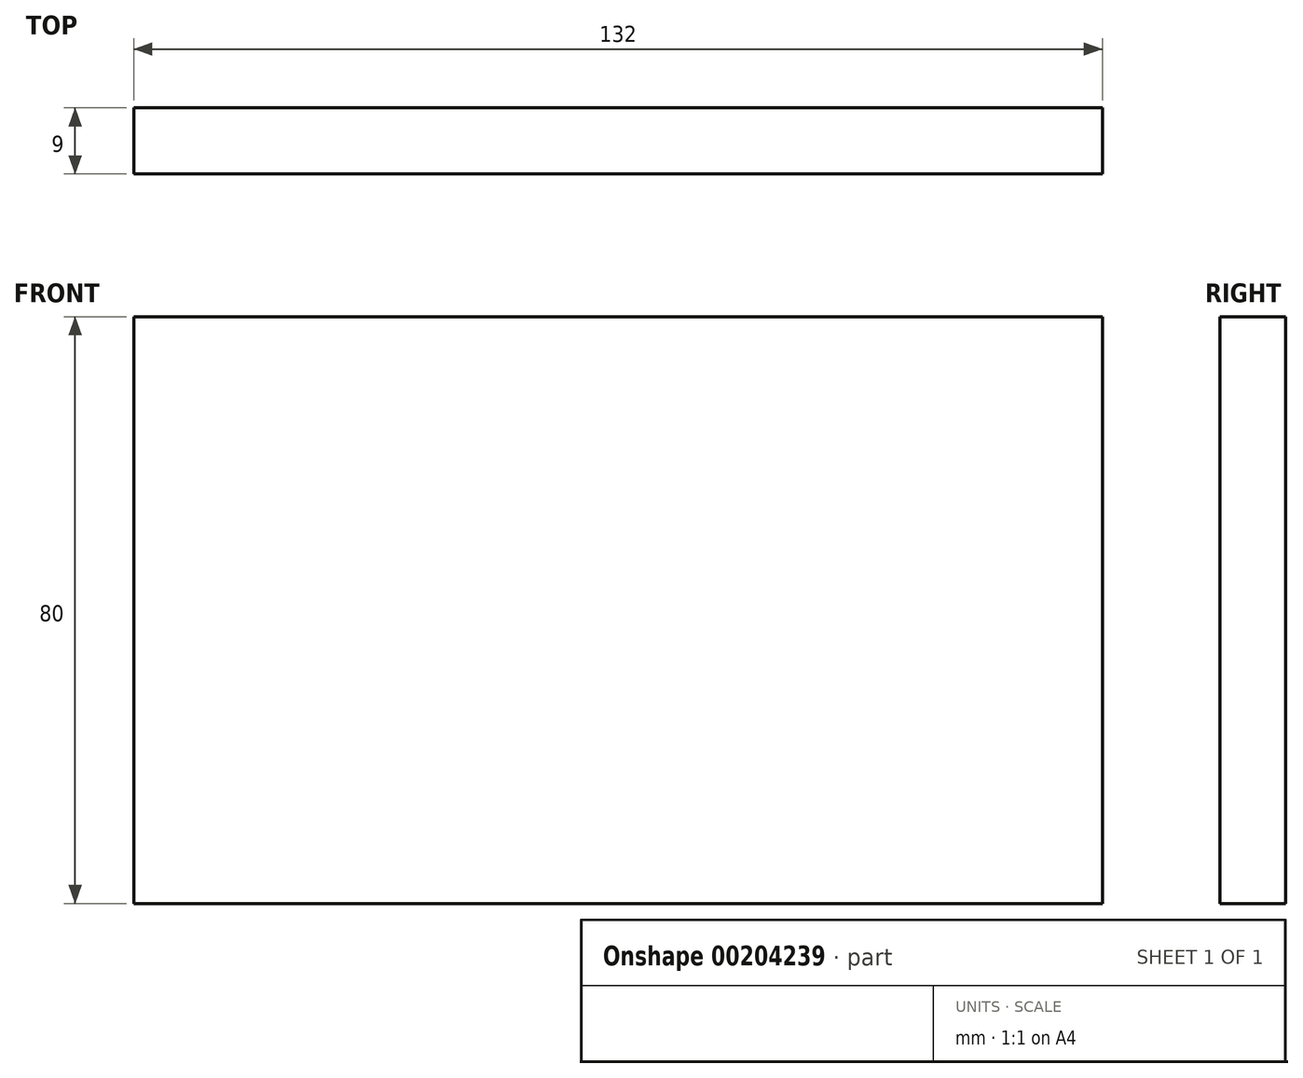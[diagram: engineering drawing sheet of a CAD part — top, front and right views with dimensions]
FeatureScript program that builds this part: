
annotation { "Feature Type Name" : "Feature", "Feature Type Description" : "" }
export const myFeature = defineFeature(function(context is Context, id is Id, definition is map)
    precondition{}
    {
        {
            var Q0;
            Q0=qCreatedBy(makeId("Front.planeOp"),FACE);
            var sketch = newSketch(context, id + "F0", { "sketchPlane" : qUnion([Q0])});
            skLineSegment(sketch, "E0.bottom", {"start": v(-58.67, 12.57) * mm, "end": v(73.33, 12.57) * mm});
            skLineSegment(sketch, "E0.top", {"start": v(-58.67, -67.43) * mm, "end": v(73.33, -67.43) * mm});
            skLineSegment(sketch, "E0.left", {"start": v(-58.67, 12.57) * mm, "end": v(-58.67, -67.43) * mm});
            skLineSegment(sketch, "E0.right", {"start": v(73.33, 12.57) * mm, "end": v(73.33, -67.43) * mm});
            skSolve(sketch);
        }
        {
            var Q0;
            Q0 = qSketchRegion(id + "F0", true);
            extrude(context, id + "F1", {"entities" : qUnion([Q0]), "depth" : 9 * mm});
        }
    });
